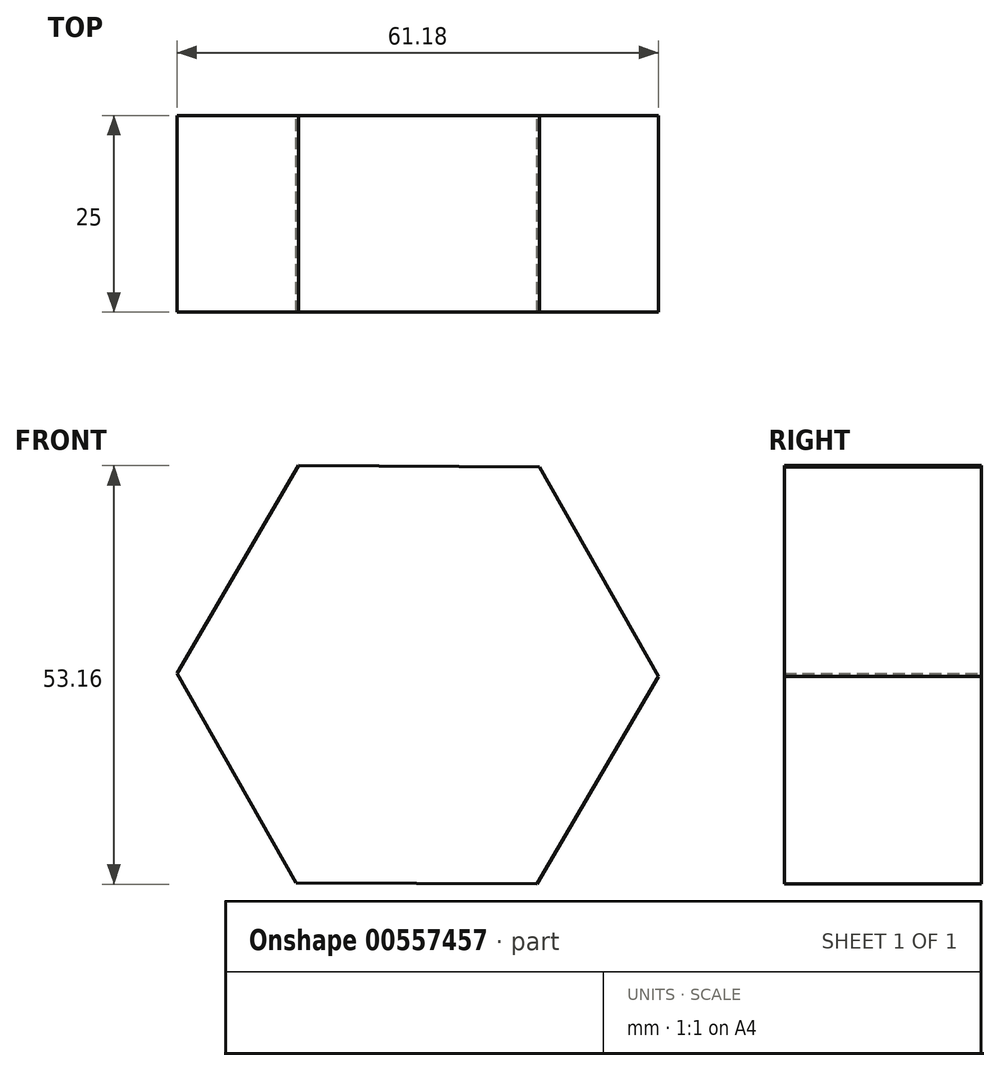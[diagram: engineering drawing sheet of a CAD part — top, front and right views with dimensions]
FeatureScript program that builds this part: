
annotation { "Feature Type Name" : "Feature", "Feature Type Description" : "" }
export const myFeature = defineFeature(function(context is Context, id is Id, definition is map)
    precondition{}
    {
        {
            var Q0;
            Q0=qCreatedBy(makeId("Front.planeOp"),FACE);
            var sketch = newSketch(context, id + "F0", { "sketchPlane" : qUnion([Q0])});
            skCircle(sketch, "E0.cCircle", {"center": v(0, 0) * mm, "radius": 26.49 * mm, "construction": true});
            skLineSegment(sketch, "E0.0", {"start": v(30.59, -0.18) * mm, "end": v(15.14, -26.58) * mm});
            skLineSegment(sketch, "E0.1", {"start": v(15.14, -26.58) * mm, "end": v(-15.45, -26.4) * mm});
            skLineSegment(sketch, "E0.2", {"start": v(-15.45, -26.4) * mm, "end": v(-30.59, 0.18) * mm});
            skLineSegment(sketch, "E0.3", {"start": v(-30.59, 0.18) * mm, "end": v(-15.14, 26.58) * mm});
            skLineSegment(sketch, "E0.4", {"start": v(-15.14, 26.58) * mm, "end": v(15.45, 26.4) * mm});
            skLineSegment(sketch, "E0.5", {"start": v(15.45, 26.4) * mm, "end": v(30.59, -0.18) * mm});
            skPoint(sketch, "E0.0.midPoint", {"position": v(22.86, -13.38) * mm});
            skSolve(sketch);
        }
        {
            var Q0;
            Q0 = qSketchRegion(id + "F0", true);
            extrude(context, id + "F1", {"entities" : qUnion([Q0]), "depth" : 25 * mm, "offsetDistance" : 25 * mm});
        }
    });
